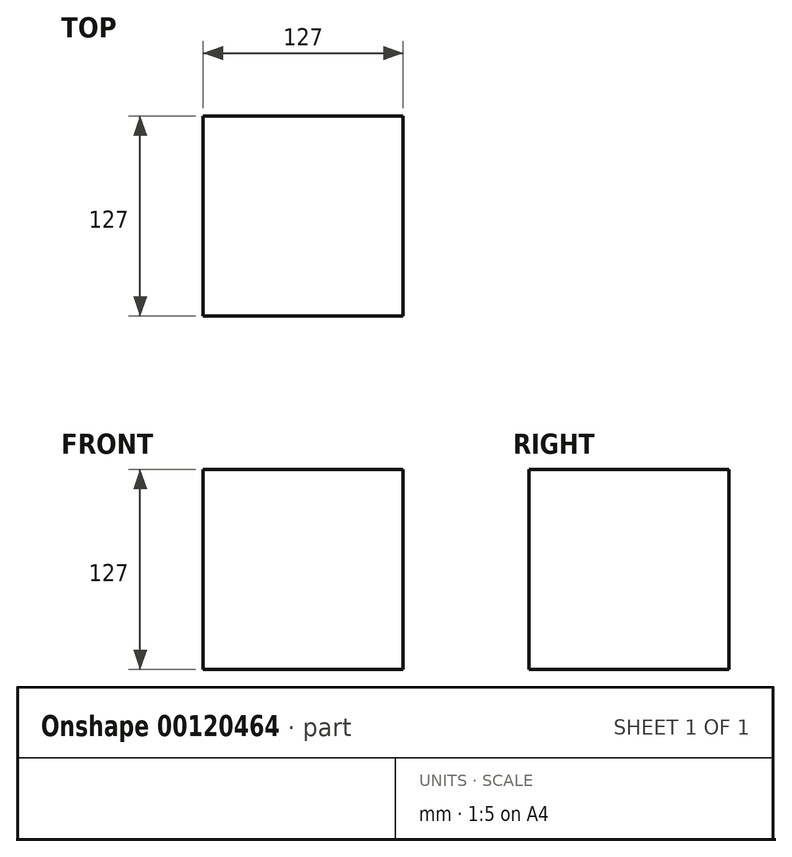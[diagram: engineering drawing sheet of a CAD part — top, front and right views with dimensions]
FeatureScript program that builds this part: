
annotation { "Feature Type Name" : "Feature", "Feature Type Description" : "" }
export const myFeature = defineFeature(function(context is Context, id is Id, definition is map)
    precondition{}
    {
        {
            var Q0;
            Q0=qCreatedBy(makeId("Top.planeOp"),FACE);
            var sketch = newSketch(context, id + "F0", { "sketchPlane" : qUnion([Q0])});
            skLineSegment(sketch, "E0.bottom", {"start": v(63.5, 63.5) * mm, "end": v(-63.5, 63.5) * mm});
            skLineSegment(sketch, "E0.top", {"start": v(63.5, -63.5) * mm, "end": v(-63.5, -63.5) * mm});
            skLineSegment(sketch, "E0.left", {"start": v(63.5, 63.5) * mm, "end": v(63.5, -63.5) * mm});
            skLineSegment(sketch, "E0.right", {"start": v(-63.5, 63.5) * mm, "end": v(-63.5, -63.5) * mm});
            skPoint(sketch, "E0.middle", {"position": v(0, 0) * mm});
            skSolve(sketch);
        }
        {
            var Q0;
            Q0=makeQuery(id+"F0.imprint","IMPRINT",FACE,{"disambiguationData":[TD([[makeQuery(id+"F0.imprint","IMPRINT",EDGE,{"derivedFrom":sQuery(id+"F0.wireOp",EDGE,"E0.bottom")}),1.0]])]});
            extrude(context, id + "F1", {"entities" : qUnion([Q0]), "depth" : 127 * mm});
        }
    });
